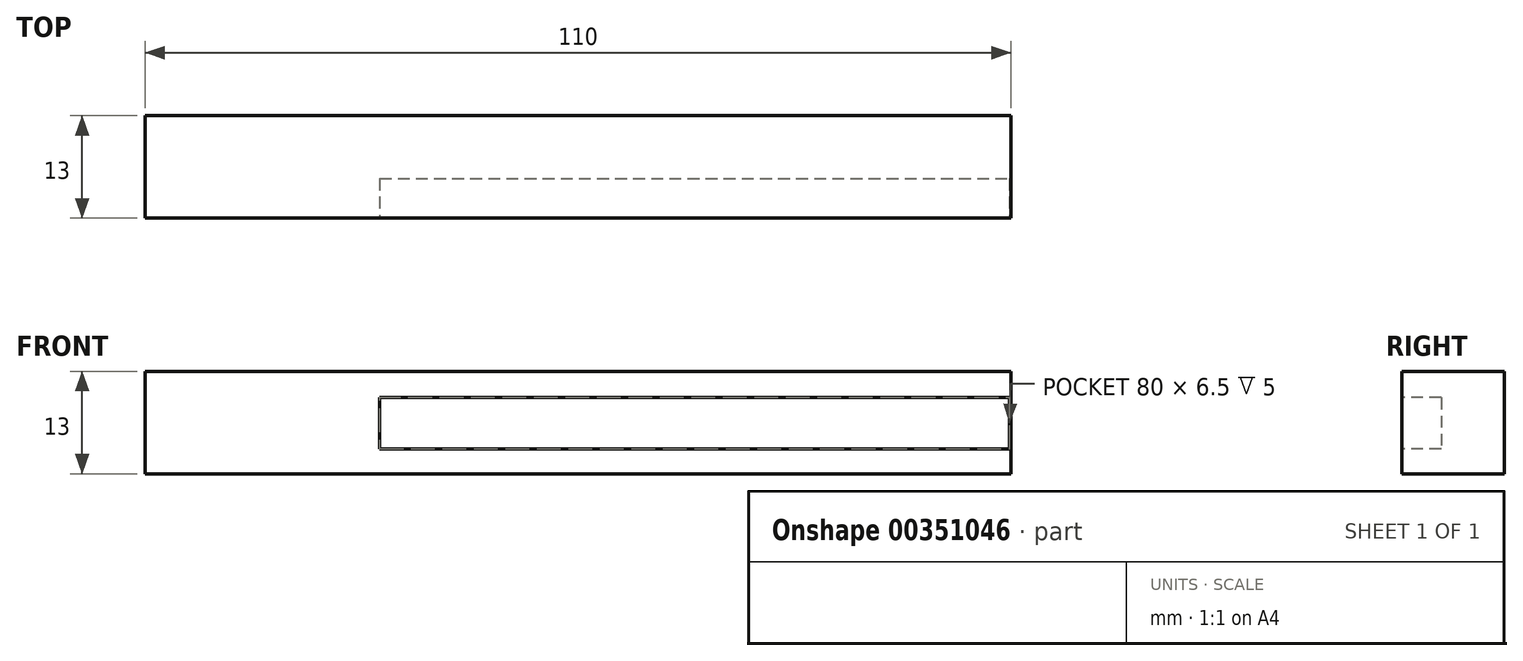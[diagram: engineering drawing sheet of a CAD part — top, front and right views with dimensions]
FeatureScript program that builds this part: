
annotation { "Feature Type Name" : "Feature", "Feature Type Description" : "" }
export const myFeature = defineFeature(function(context is Context, id is Id, definition is map)
    precondition{}
    {
        {
            var Q0;
            Q0=qCreatedBy(makeId("Right.planeOp"),FACE);
            var sketch = newSketch(context, id + "F0", { "sketchPlane" : qUnion([Q0])});
            skLineSegment(sketch, "E0.bottom", {"start": v(-6.5, 6.5) * mm, "end": v(6.5, 6.5) * mm});
            skLineSegment(sketch, "E0.top", {"start": v(-6.5, -6.5) * mm, "end": v(6.5, -6.5) * mm});
            skLineSegment(sketch, "E0.left", {"start": v(-6.5, 6.5) * mm, "end": v(-6.5, -6.5) * mm});
            skLineSegment(sketch, "E0.right", {"start": v(6.5, 6.5) * mm, "end": v(6.5, -6.5) * mm});
            skSolve(sketch);
        }
        {
            var Q0;
            Q0 = qSketchRegion(id + "F0", true);
            extrude(context, id + "F1", {"entities" : qUnion([Q0]), "depth" : 110 * mm});
        }
        {
            var Q0;
            Q0=makeQuery(id+"F1.opExtrude","SWEPT_FACE",FACE,{"disambiguationData":[OSD([sQuery(id+"F0.wireOp",EDGE,"E0.left")])]});
            var sketch = newSketch(context, id + "F2", { "sketchPlane" : qUnion([Q0])});
            skLineSegment(sketch, "E1.bottom", {"start": v(29.81, 3.18) * mm, "end": v(109.81, 3.18) * mm});
            skLineSegment(sketch, "E1.top", {"start": v(29.81, -3.32) * mm, "end": v(109.81, -3.32) * mm});
            skLineSegment(sketch, "E1.left", {"start": v(29.81, 3.18) * mm, "end": v(29.81, -3.32) * mm});
            skLineSegment(sketch, "E1.right", {"start": v(109.81, 3.18) * mm, "end": v(109.81, -3.32) * mm});
            skSolve(sketch);
        }
        {
            var Q0;
            Q0=makeQuery(id+"F2.imprint","IMPRINT",FACE,{"disambiguationData":[TD([[makeQuery(id+"F2.imprint","IMPRINT",EDGE,{"derivedFrom":sQuery(id+"F2.wireOp",EDGE,"E1.bottom")}),-1.0]])]});
            extrude(context, id + "F3", {"entities" : qUnion([Q0]), "operationType" : NewBodyOperationType.REMOVE, "oppositeDirection" : true, "depth" : 5 * mm});
        }
    });
